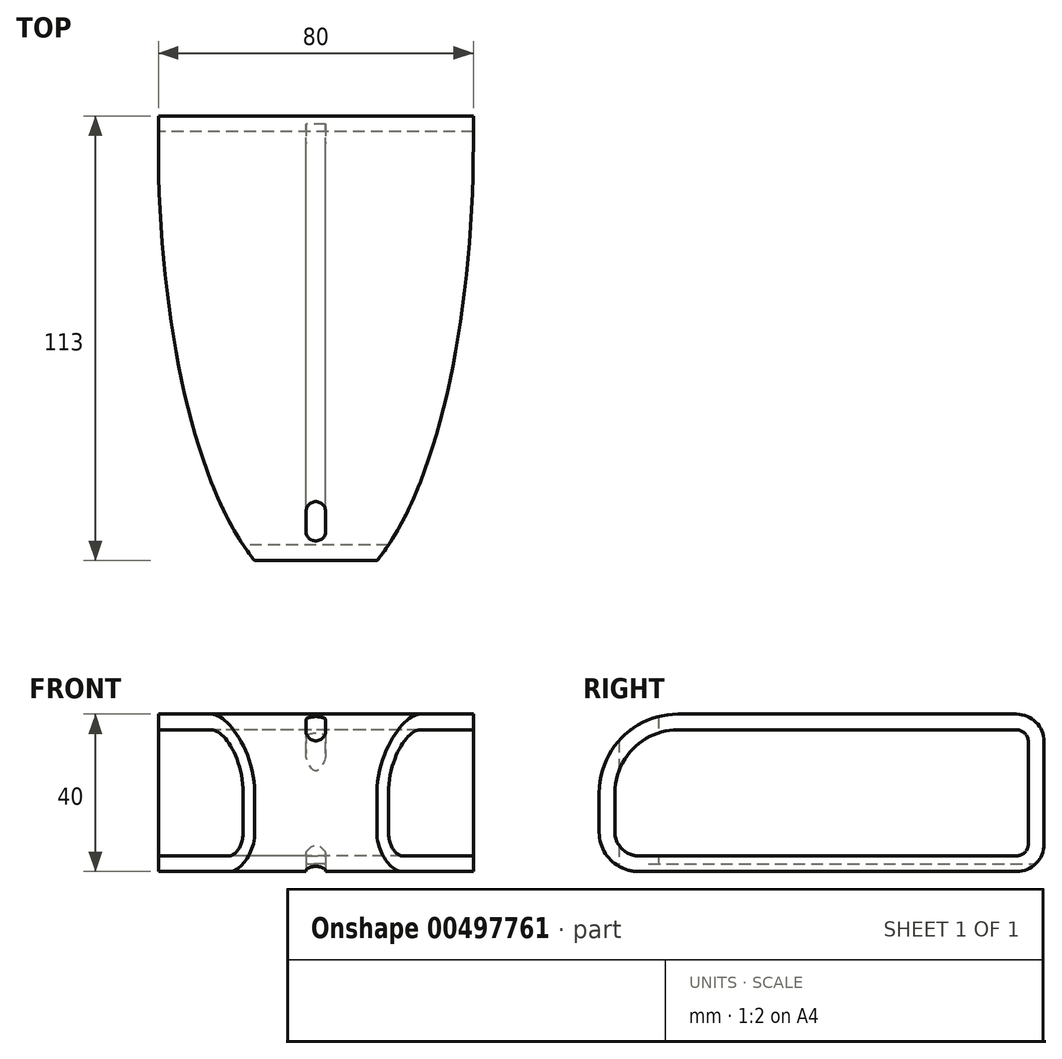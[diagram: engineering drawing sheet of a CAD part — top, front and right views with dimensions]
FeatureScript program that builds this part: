
annotation { "Feature Type Name" : "Feature", "Feature Type Description" : "" }
export const myFeature = defineFeature(function(context is Context, id is Id, definition is map)
    precondition{}
    {
        {
            var Q0;
            Q0=qCreatedBy(makeId("Right.planeOp"),FACE);
            var sketch = newSketch(context, id + "F0", { "sketchPlane" : qUnion([Q0])});
            skLineSegment(sketch, "E0", {"start": v(0, 0) * mm, "end": v(-96, 0) * mm});
            skLineSegment(sketch, "E1", {"start": v(-106, 10) * mm, "end": v(-106, 20) * mm});
            skLineSegment(sketch, "E2", {"start": v(-86, 40) * mm, "end": v(0, 40) * mm});
            skPoint(sketch, "E3.visualSharp", {"position": v(-106, 0) * mm});
            skArc(sketch, "E3.filletArc", {"start": v(-106, 10) * mm, "mid": v(-103.07, 2.93) * mm, "end": v(-96, 0) * mm});
            skPoint(sketch, "E4.visualSharp", {"position": v(-106, 40) * mm});
            skArc(sketch, "E4.filletArc", {"start": v(-86, 40) * mm, "mid": v(-100.14, 34.14) * mm, "end": v(-106, 20) * mm});
            skLineSegment(sketch, "E5.0", {"start": v(-86, 36) * mm, "end": v(0, 36) * mm});
            skLineSegment(sketch, "E5.1", {"start": v(0, 4) * mm, "end": v(-96, 4) * mm});
            skArc(sketch, "E5.2", {"start": v(-102, 10) * mm, "mid": v(-100.24, 5.76) * mm, "end": v(-96, 4) * mm});
            skLineSegment(sketch, "E5.3", {"start": v(-102, 10) * mm, "end": v(-102, 20) * mm});
            skArc(sketch, "E5.4", {"start": v(-86, 36) * mm, "mid": v(-97.31, 31.31) * mm, "end": v(-102, 20) * mm});
            skArc(sketch, "E6", {"start": v(3, 33) * mm, "mid": v(2.12, 35.12) * mm, "end": v(0, 36) * mm});
            skArc(sketch, "E7", {"start": v(0, 4) * mm, "mid": v(2.12, 4.88) * mm, "end": v(3, 7) * mm});
            skArc(sketch, "E8", {"start": v(7, 33) * mm, "mid": v(4.95, 37.95) * mm, "end": v(0, 40) * mm});
            skArc(sketch, "E9", {"start": v(0, 0) * mm, "mid": v(4.95, 2.05) * mm, "end": v(7, 7) * mm});
            skLineSegment(sketch, "E10", {"start": v(7, 33) * mm, "end": v(0, 33) * mm, "construction": true});
            skLineSegment(sketch, "E11", {"start": v(0, 7) * mm, "end": v(7, 7) * mm, "construction": true});
            skLineSegment(sketch, "E12", {"start": v(7, 33) * mm, "end": v(7, 7) * mm});
            skLineSegment(sketch, "E13", {"start": v(3, 33) * mm, "end": v(3, 7) * mm});
            skSolve(sketch);
        }
        {
            var Q0;
            Q0=makeQuery(id+"F0.imprint","IMPRINT",FACE,{"disambiguationData":[TD([[makeQuery(id+"F0.imprint","IMPRINT",EDGE,{"derivedFrom":sQuery(id+"F0.wireOp",EDGE,"E0")}),-1.0]])]});
            extrude(context, id + "F1", {"entities" : qUnion([Q0]), "depth" : 40 * mm, "hasSecondDirection" : true, "secondDirectionOppositeDirection" : true, "secondDirectionDepth" : 40 * mm});
        }
        {
            var Q0;
            Q0=makeQuery(id+"F1.opExtrude","SWEPT_FACE",FACE,{"disambiguationData":[OSD([sQuery(id+"F0.wireOp",EDGE,"E2")])]});
            var sketch = newSketch(context, id + "F2", { "sketchPlane" : qUnion([Q0])});
            skEllipticalArc(sketch, "E14", {});
            skLineSegment(sketch, "E15", {"start": v(-40, 0) * mm, "end": v(-40, -106) * mm});
            skLineSegment(sketch, "E16.0", {"start": v(40, -106) * mm, "end": v(15.51, -106) * mm});
            skLineSegment(sketch, "E17", {"start": v(40, -106) * mm, "end": v(40, 0) * mm});
            skLineSegment(sketch, "E18.trimOffspring", {"start": v(-15.51, -106) * mm, "end": v(-40, -106) * mm});
            skEllipticalArc(sketch, "E19.trimOffspring", {});
            const initialGuessF2  = {"E14": [0, 0, 1, 0, 0.04, 0.115, 5.110643969822942, 6.283185307179586], "E19.trimOffspring": [0, 0, 1, 0, 0.04, 0.115, 3.141592653589793, 4.314133990946438]};
            skSetInitialGuess(sketch, initialGuessF2);
            skSolve(sketch);
        }
        {
            var Q0;
            Q0 = qSketchRegion(id + "F2", true);
            var Q1;
            Q1=makeQuery(id+"F1.opExtrude","SWEPT_FACE",FACE,{"disambiguationData":[OSD([sQuery(id+"F0.wireOp",EDGE,"E0")])]});
            extrude(context, id + "F3", {"entities" : qUnion([Q0]), "operationType" : NewBodyOperationType.REMOVE, "endBound" : BoundingType.UP_TO_SURFACE, "oppositeDirection" : true, "endBoundEntityFace" : qUnion([Q1]), "depth" : 25 * mm});
        }
        {
            var Q0;
            Q0=makeQuery(id+"F1.opExtrude","SWEPT_FACE",FACE,{"disambiguationData":[OSD([sQuery(id+"F0.wireOp",EDGE,"E0")])]});
            var sketch = newSketch(context, id + "F4", { "sketchPlane" : qUnion([Q0])});
            skPoint(sketch, "E20.0", {"position": v(0, 98.5) * mm});
            skArc(sketch, "E21", {"start": v(2.5, 98.5) * mm, "mid": v(0, 101) * mm, "end": v(-2.5, 98.5) * mm});
            skArc(sketch, "E22", {"start": v(-2.5, 93.5) * mm, "mid": v(0, 91) * mm, "end": v(2.5, 93.5) * mm});
            skLineSegment(sketch, "E23", {"start": v(-2.5, 98.5) * mm, "end": v(-2.5, 93.5) * mm});
            skLineSegment(sketch, "E24", {"start": v(2.5, 98.5) * mm, "end": v(2.5, 93.5) * mm});
            skSolve(sketch);
        }
        {
            var Q0;
            Q0 = qSketchRegion(id + "F4", true);
            extrude(context, id + "F5", {"entities" : qUnion([Q0]), "operationType" : NewBodyOperationType.REMOVE, "endBound" : BoundingType.THROUGH_ALL, "oppositeDirection" : true, "depth" : 25 * mm});
        }
        {
            var Q0;
            Q0=qCreatedBy(makeId("Front.planeOp"),FACE);
            var sketch = newSketch(context, id + "F6", { "sketchPlane" : qUnion([Q0])});
            skLineSegment(sketch, "E25.bottom", {"start": v(2.5, 0) * mm, "end": v(-2.5, 0) * mm});
            skLineSegment(sketch, "E25.top", {"start": v(2.5, 2) * mm, "end": v(-2.5, 2) * mm});
            skLineSegment(sketch, "E25.left", {"start": v(2.5, 0) * mm, "end": v(2.5, 2) * mm});
            skLineSegment(sketch, "E25.right", {"start": v(-2.5, 0) * mm, "end": v(-2.5, 2) * mm});
            skSolve(sketch);
        }
        {
            var Q0;
            Q0 = qSketchRegion(id + "F6", true);
            var Q1;
            Q1=makeQuery(id+"F1.opExtrude","SWEPT_FACE",FACE,{"disambiguationData":[OSD([sQuery(id+"F0.wireOp",EDGE,"E12")])]});
            extrude(context, id + "F7", {"entities" : qUnion([Q0]), "operationType" : NewBodyOperationType.REMOVE, "depth" : 95 * mm, "offsetDistance" : 25 * mm, "hasSecondDirection" : true, "secondDirectionBound" : SecondDirectionBoundingType.UP_TO_SURFACE, "secondDirectionOppositeDirection" : true, "secondDirectionDepth" : 25 * mm, "secondDirectionBoundEntityFace" : qUnion([Q1])});
        }
        {
            var Q0;
            Q0 = qSketchRegion(id + "F2", true);
            var Q1;
            {var subQ5=sQuery(id+"F0.wireOp",EDGE,"E0");var subQ6=makeQuery(id+"F1.opExtrude","SWEPT_FACE",FACE,{"disambiguationData":[OSD([subQ5])]});Q1=makeQuery(id+"F7.boolean.opBoolean","SPLIT",FACE,{"disambiguationData":[TD([makeQuery(id+"F3.boolean.opBoolean","COPY",FACE,{"derivedFrom":makeQuery(id+"F3.opExtrude","SWEPT_FACE",FACE,{"disambiguationData":[OSD([sQuery(id+"F2.wireOp",EDGE,"E14")])]})})])],"derivedFrom":subQ6});}
            extrude(context, id + "F8", {"entities" : qUnion([Q0]), "operationType" : NewBodyOperationType.REMOVE, "endBound" : BoundingType.UP_TO_SURFACE, "oppositeDirection" : true, "depth" : 25 * mm, "endBoundEntityFace" : qUnion([Q1]), "offsetDistance" : 25 * mm});
        }
    });
